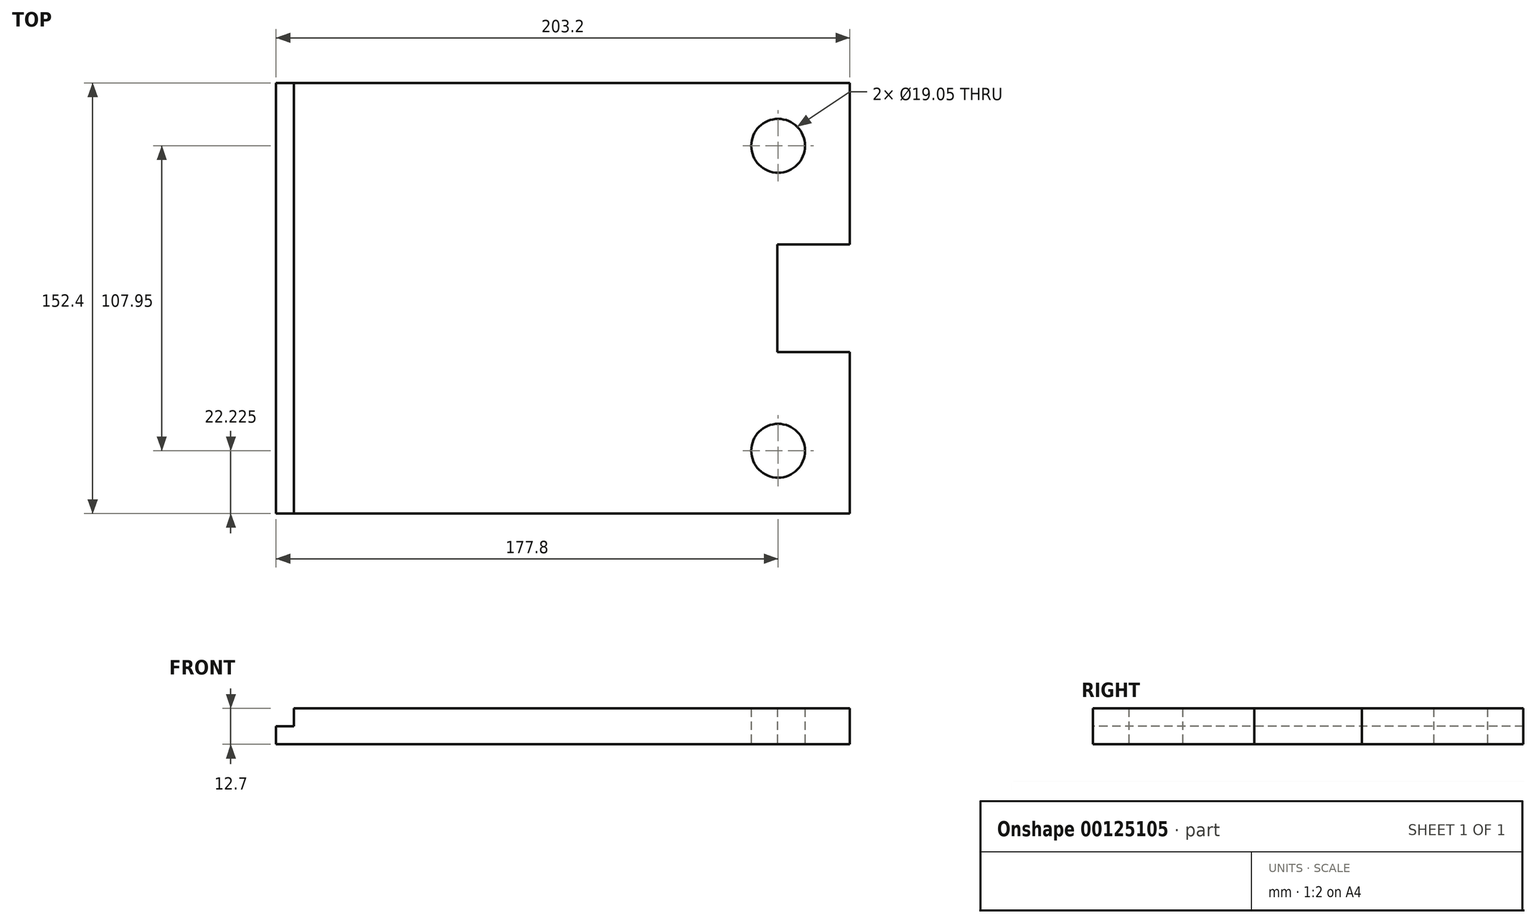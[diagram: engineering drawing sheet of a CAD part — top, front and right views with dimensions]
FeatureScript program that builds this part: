
annotation { "Feature Type Name" : "Feature", "Feature Type Description" : "" }
export const myFeature = defineFeature(function(context is Context, id is Id, definition is map)
    precondition{}
    {
        {
            var Q0;
            Q0=qCreatedBy(makeId("Top.planeOp"),FACE);
            var sketch = newSketch(context, id + "F0", { "sketchPlane" : qUnion([Q0])});
            skLineSegment(sketch, "E0.bottom", {"start": v(-101.6, 76.2) * mm, "end": v(101.6, 76.2) * mm});
            skLineSegment(sketch, "E0.top", {"start": v(-101.6, -76.2) * mm, "end": v(101.6, -76.2) * mm});
            skLineSegment(sketch, "E0.left", {"start": v(-101.6, 76.2) * mm, "end": v(-101.6, -76.2) * mm});
            skLineSegment(sketch, "E0.right", {"start": v(101.6, 76.2) * mm, "end": v(101.6, -76.2) * mm});
            skPoint(sketch, "E0.middle", {"position": v(0, 0) * mm});
            skCircle(sketch, "E1", {"center": v(76.2, 53.98) * mm, "radius": 9.53 * mm});
            skCircle(sketch, "E2.MirrorC", {"center": v(76.2, -53.98) * mm, "radius": 9.53 * mm});
            skLineSegment(sketch, "E3.bottom", {"start": v(75.86, 19.05) * mm, "end": v(127.34, 19.05) * mm});
            skLineSegment(sketch, "E3.top", {"start": v(75.86, -19.05) * mm, "end": v(127.34, -19.05) * mm});
            skLineSegment(sketch, "E3.left", {"start": v(75.86, 19.05) * mm, "end": v(75.86, -19.05) * mm});
            skPoint(sketch, "E3.middle", {"position": v(101.6, 0) * mm});
            skSolve(sketch);
        }
        {
            var Q0;
            {var subQ1=sQuery(id+"F0.wireOp",EDGE,"E0.bottom");Q0=makeQuery(id+"F0.imprint","IMPRINT",FACE,{"disambiguationData":[TD([[makeQuery(id+"F0.imprint","IMPRINT",EDGE,{"derivedFrom":subQ1}),-1.0]])]});}
            extrude(context, id + "F1", {"entities" : qUnion([Q0]), "depth" : 12.7 * mm});
        }
        {
            var Q0;
            Q0=makeQuery(id+"F1.opExtrude","SWEPT_FACE",FACE,{"disambiguationData":[OSD([sQuery(id+"F0.wireOp",EDGE,"E0.top")])]});
            var sketch = newSketch(context, id + "F2", { "sketchPlane" : qUnion([Q0])});
            skLineSegment(sketch, "E4.bottom", {"start": v(-101.6, 12.7) * mm, "end": v(-95.25, 12.7) * mm});
            skLineSegment(sketch, "E4.top", {"start": v(-101.6, 6.35) * mm, "end": v(-95.25, 6.35) * mm});
            skLineSegment(sketch, "E4.left", {"start": v(-101.6, 12.7) * mm, "end": v(-101.6, 6.35) * mm});
            skLineSegment(sketch, "E4.right", {"start": v(-95.25, 12.7) * mm, "end": v(-95.25, 6.35) * mm});
            skSolve(sketch);
        }
        {
            var Q0;
            Q0=makeQuery(id+"F2.imprint","IMPRINT",FACE,{"disambiguationData":[TD([[makeQuery(id+"F2.imprint","IMPRINT",EDGE,{"derivedFrom":sQuery(id+"F2.wireOp",EDGE,"E4.bottom")}),-1.0]])]});
            extrude(context, id + "F3", {"entities" : qUnion([Q0]), "operationType" : NewBodyOperationType.REMOVE, "endBound" : BoundingType.THROUGH_ALL, "oppositeDirection" : true, "depth" : 152.4 * mm});
        }
    });
